# Revit family: Grohe_PlumbingFixture_EuphoriaSystem260_ShowerSystem_272960031
name_source: partatom
category: Plumbing Fixtures
revit_build: Autodesk Revit 2018 (Build: 20190510_1515(x64)
units: mm (PartAtom-declared; Revit-internal decimal feet)

## family parameters
Cut with Voids When Loaded = No
Host = Face
OmniClass Number = 23.45.05.14.17
OmniClass Title = Showers
Part Type = Normal
Room Calculation Point = No
Round Connector Dimension = Use Diameter
Shared = No

## types (1)
- 27296003
    ADACompliant = No
    Assembly Code = D2010710
    AssetType = Fixed
    BIMObjectName = Grohe_PlumbingFixture_EuphoriaSystem260_ShowerSystem_27296003
    CW Connection = Yes
    CWFU = 4.5
    ClassificationName = Uniclass 2015
    ClassificationValue = Pr_40_20_87_76
    ColdWaterConnectionDiameter = 13 mm  [stored 0.0426509 ft]
    Cost = 0 $
    Default Elevation = 0 mm  [stored 0 ft]
    Description = Euphoria System 260
    DocumentationCertificates = www.bimstore.co
    DocumentationInstallationGuide = www.bimstore.co
    DocumentationLiterature = www.bimstore.co
    DocumentationMaintenance = www.bimstore.co
    DocumentationTechnical = www.bimstore.co
    DurationUnit = Years
    Ecojoy = No
    ExpectedLife = 0
    Features = Shower system with thermoststic mixer for wall mounting Consisting of: horizontal swivable 450 mm projection shower arm exposed thermostatic shower with Aquadimmer function allows change between: head shower Euphoria 260 (26 455) Rain, SmartRain, Jet with ball joint rotation angle ± 15° hand shower Euphoria 110 Massage  (27 221 000) 3 spray patterns: Rain, Massage, SmartRain adjustable height via gliding element Silverflex shower hose 1750 mm (28 388 000) GROHE TurboStat compact cartridge with wax thermoelement GROHE SafeStop safety button at 38°C  ( calibration required ) GROHE SafeStop Plus optional temperature limiter at 43°C included GROHE CoolTouch prevents scalding on hot surfaces GROHE DreamSpray perfect spray pattern GROHE StarLight chrome finish GROHE SprayDimmer (Stepless  flow rate reduction) GROHE ProGrip with knurl structure GROHE FastFixation (upper bracket adjustable) Inner WaterGuide for a longer life SpeedClean anti-limescale system Twistfree preventing the hose from twisting suitable for instantaneous heaters from 18 kW/h minimum flow rate 7 l/min. min. recommended pressure 1 bar optional upgrade: GROHE EasyReach tray (26 362) professional edition
    Finish = Chrome
    HW Connection = Yes
    HWFU = 4.5
    HotWaterConnectionDiameter = 13 mm  [stored 0.0426509 ft]
    IfcExportAs = IfcPipeFitting
    IfcExportType = IfcPipeFittingType
    Keynote = N13
    LowEmittingMaterial = No
    Manufacturer = Grohe
    ManufacturerName = Grohe
    MasterformatNumber = 01 52 19
    MasterformatTitle = Sanitary Facilities
    Model = Euphoria System 260
    ModelNumber = 27296003
    ModelReference = Euphoria System 260
    NBSDescription = Shower heads
    NBSObjectName = Grohe - Shower heads
    NBSReference = 45-35-70/333
    NominalDepth = 0 mm  [stored 0 ft]
    NominalHeight = 0 mm  [stored 0 ft]
    NominalLength = 0 mm  [stored 0 ft]
    PipeMaterial = GroheLimited-Pipework
    PrimaryMaterial = Grohe-Chrome
    ProductionYear = 2020
    Type Comments = 27296003
    TypeName = 27296003
    URL = www.grohe.com
    WFU = 0
    WarrantyDurationLabor = 0
    WarrantyDurationParts = 0
    WarrantyDurationUnit = Years
    _BSBibleVersion = 16
    _BimSpecGuid = 0
    _CurrentRevision = 1
    _DistributedBy = www.bimstore.co
    _ObjectUserGuide = www.bimstore.co

note: [stored X ft] marks values corroborated as IEEE doubles in the binary element streams (Revit-internal decimal feet)

## geometry (parser evidence)
native form markers: Sweep x2
no freeform markers — native parametric forms only
